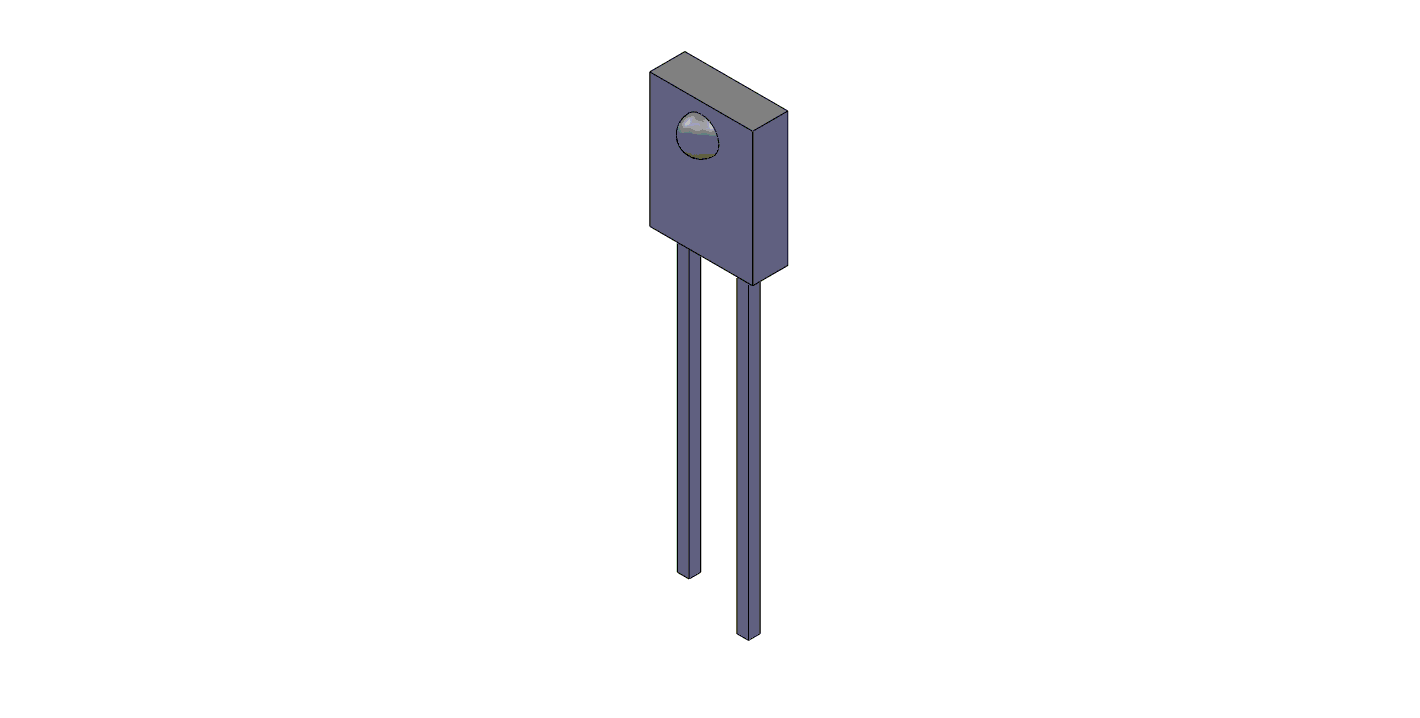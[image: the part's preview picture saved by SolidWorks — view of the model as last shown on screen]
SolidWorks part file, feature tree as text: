
SOLIDWORKS PART (.sldprt)
format: sldprt  version: not decoded by parser v0  size: 137,728 bytes
history: native  units: mm
features: sketch x3, extrude x2, material x1, revolve x1 (+12 scaffold rows collapsed)
feature tree (19):
  scaffold x12  (default folders/planes/origin — collapsed)
  material  "Material <not specified>"
  sketch  "Sketch1"  dims[D1=4.3942mm D2=5.715mm]
  extrude  "Boss-Extrude1"  Depth=1.4986mm
  sketch  "Sketch3"  dims[D1=1.22mm D2=0.75mm]
  revolve  "Revolve1"  Angle=360deg
  sketch  "Sketch4"  dims[D1=2.54mm D2=0.5mm D3=12.7mm D4=1.0mm]
  extrude  "Boss-Extrude2"  Depth=0.5mm
decode coverage: 6 of 6 modeling features carry decoded parameters
note: suppression state not decoded; provenance and decode notes live in map.json
